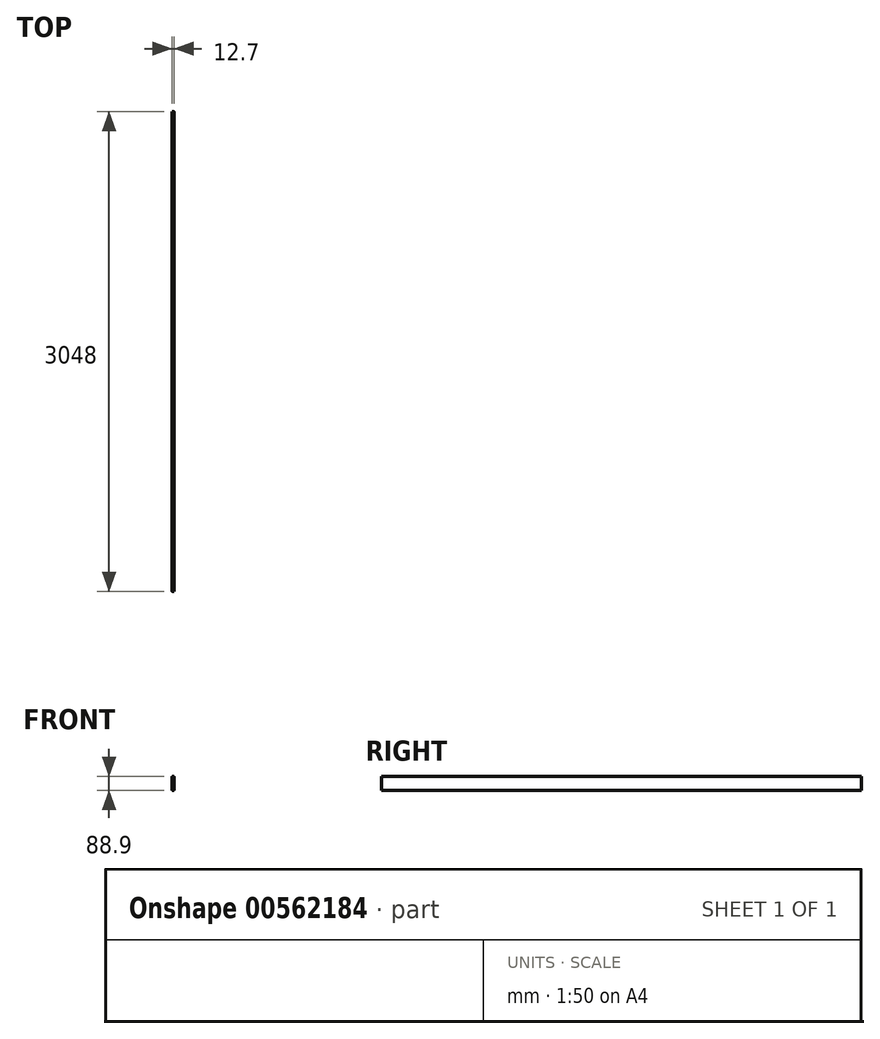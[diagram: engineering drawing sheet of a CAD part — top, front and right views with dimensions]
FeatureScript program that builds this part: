
annotation { "Feature Type Name" : "Feature", "Feature Type Description" : "" }
export const myFeature = defineFeature(function(context is Context, id is Id, definition is map)
    precondition{}
    {
        {
            var Q0;
            Q0=qCreatedBy(makeId("Front.planeOp"),FACE);
            var sketch = newSketch(context, id + "F0", { "sketchPlane" : qUnion([Q0])});
            skLineSegment(sketch, "E0.bottom", {"start": v(-3.17, 44.45) * mm, "end": v(3.17, 44.45) * mm});
            skLineSegment(sketch, "E0.top", {"start": v(-3.17, -44.45) * mm, "end": v(3.17, -44.45) * mm});
            skLineSegment(sketch, "E0.left", {"start": v(-6.35, 41.28) * mm, "end": v(-6.35, -41.28) * mm});
            skLineSegment(sketch, "E0.right", {"start": v(6.35, 41.28) * mm, "end": v(6.35, -41.28) * mm});
            skPoint(sketch, "E1.visualSharp", {"position": v(-6.35, 44.45) * mm});
            skArc(sketch, "E1.filletArc", {"start": v(-3.17, 44.45) * mm, "mid": v(-5.42, 43.52) * mm, "end": v(-6.35, 41.28) * mm});
            skPoint(sketch, "E2.visualSharp", {"position": v(6.35, 44.45) * mm});
            skArc(sketch, "E2.filletArc", {"start": v(6.35, 41.28) * mm, "mid": v(5.42, 43.52) * mm, "end": v(3.17, 44.45) * mm});
            skPoint(sketch, "E3.visualSharp", {"position": v(-6.35, -44.45) * mm});
            skArc(sketch, "E3.filletArc", {"start": v(-6.35, -41.28) * mm, "mid": v(-5.42, -43.52) * mm, "end": v(-3.17, -44.45) * mm});
            skPoint(sketch, "E4.visualSharp", {"position": v(6.35, -44.45) * mm});
            skArc(sketch, "E4.filletArc", {"start": v(3.17, -44.45) * mm, "mid": v(5.42, -43.52) * mm, "end": v(6.35, -41.28) * mm});
            skLineSegment(sketch, "E5", {"start": v(0, 0) * mm, "end": v(0, -44.45) * mm, "construction": true});
            skLineSegment(sketch, "E6", {"start": v(0, 0) * mm, "end": v(-6.35, 0) * mm, "construction": true});
            skSolve(sketch);
        }
        {
            var Q0;
            Q0=makeQuery(id+"F0.imprint","IMPRINT",FACE,{"disambiguationData":[TD([[makeQuery(id+"F0.imprint","IMPRINT",EDGE,{"derivedFrom":sQuery(id+"F0.wireOp",EDGE,"E0.bottom")}),-1.0]])]});
            extrude(context, id + "F1", {"entities" : qUnion([Q0]), "depth" : 3048 * mm, "offsetDistance" : 25.4 * mm});
        }
    });
